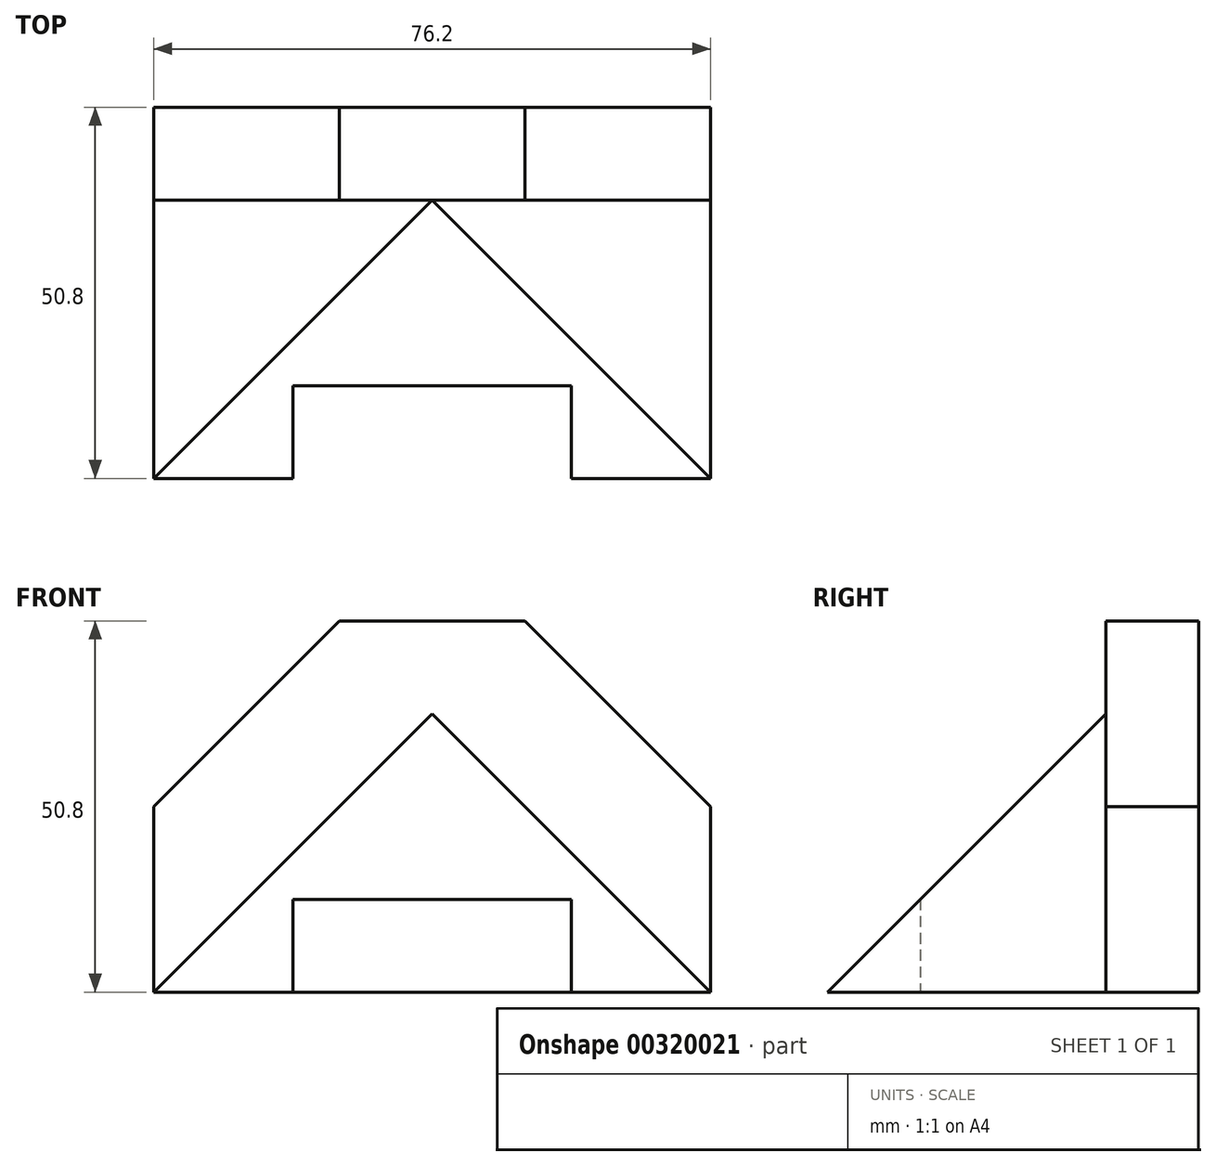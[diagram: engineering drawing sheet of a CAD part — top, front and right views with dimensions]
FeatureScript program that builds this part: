
annotation { "Feature Type Name" : "Feature", "Feature Type Description" : "" }
export const myFeature = defineFeature(function(context is Context, id is Id, definition is map)
    precondition{}
    {
        {
            var Q0;
            Q0=qCreatedBy(makeId("Front.planeOp"),FACE);
            var sketch = newSketch(context, id + "F0", { "sketchPlane" : qUnion([Q0])});
            skLineSegment(sketch, "E0", {"start": v(0, 0) * mm, "end": v(0, 25.4) * mm});
            skLineSegment(sketch, "E1", {"start": v(0, 25.4) * mm, "end": v(25.4, 50.8) * mm});
            skLineSegment(sketch, "E2", {"start": v(25.4, 50.8) * mm, "end": v(50.8, 50.8) * mm});
            skLineSegment(sketch, "E3", {"start": v(50.8, 50.8) * mm, "end": v(76.2, 25.4) * mm});
            skLineSegment(sketch, "E4", {"start": v(76.2, 25.4) * mm, "end": v(76.2, 0) * mm});
            skLineSegment(sketch, "E5", {"start": v(76.2, 0) * mm, "end": v(0, 0) * mm});
            skSolve(sketch);
        }
        {
            var Q0;
            Q0 = qSketchRegion(id + "F0", true);
            extrude(context, id + "F1", {"entities" : qUnion([Q0]), "depth" : 12.7 * mm});
        }
        {
            var Q0;
            Q0=makeQuery(id+"F1.opExtrude","CAP_FACE",FACE,{"disambiguationData":[OSD([sQuery(id+"F0.wireOp",EDGE,"E0"),sQuery(id+"F0.wireOp",EDGE,"E1"),sQuery(id+"F0.wireOp",EDGE,"E2"),sQuery(id+"F0.wireOp",EDGE,"E3"),sQuery(id+"F0.wireOp",EDGE,"E4"),sQuery(id+"F0.wireOp",EDGE,"E5")])],"isStart":false});
            var sketch = newSketch(context, id + "F2", { "sketchPlane" : qUnion([Q0])});
            skLineSegment(sketch, "E6", {"start": v(0, 0) * mm, "end": v(76.2, 0) * mm});
            skLineSegment(sketch, "E7", {"start": v(76.2, 0) * mm, "end": v(38.1, 38.1) * mm});
            skLineSegment(sketch, "E8", {"start": v(38.1, 38.1) * mm, "end": v(0, 0) * mm});
            skSolve(sketch);
        }
        {
            var Q0;
            Q0 = qSketchRegion(id + "F2", true);
            extrude(context, id + "F3", {"entities" : qUnion([Q0]), "operationType" : NewBodyOperationType.ADD, "depth" : 38.1 * mm});
        }
        {
            var Q0;
            Q0=makeQuery(id+"F1.opExtrude","SWEPT_FACE",FACE,{"disambiguationData":[OSD([sQuery(id+"F0.wireOp",EDGE,"E4")])]});
            var sketch = newSketch(context, id + "F4", { "sketchPlane" : qUnion([Q0])});
            skLineSegment(sketch, "E9", {"start": v(-50.8, 0) * mm, "end": v(-12.7, 38.1) * mm});
            skLineSegment(sketch, "E10", {"start": v(-12.7, 38.1) * mm, "end": v(-50.8, 38.1) * mm});
            skLineSegment(sketch, "E11", {"start": v(-50.8, 38.1) * mm, "end": v(-50.8, 0) * mm});
            skSolve(sketch);
        }
        {
            var Q0;
            Q0 = qSketchRegion(id + "F4", true);
            extrude(context, id + "F5", {"entities" : qUnion([Q0]), "operationType" : NewBodyOperationType.REMOVE, "endBound" : BoundingType.THROUGH_ALL, "oppositeDirection" : true, "depth" : 25.4 * mm});
        }
        {
            var Q0;
            Q0=makeQuery(id+"F3.boolean.opBoolean","MERGE",FACE,{"derivedFrom":[makeQuery(id+"F1.opExtrude","SWEPT_FACE",FACE,{"disambiguationData":[OSD([sQuery(id+"F0.wireOp",EDGE,"E5")])]}),makeQuery(id+"F3.opExtrude","SWEPT_FACE",FACE,{"disambiguationData":[OSD([sQuery(id+"F2.wireOp",EDGE,"E6")])]})]});
            var sketch = newSketch(context, id + "F6", { "sketchPlane" : qUnion([Q0])});
            skLineSegment(sketch, "E12", {"start": v(19.05, 50.8) * mm, "end": v(19.05, 38.1) * mm});
            skLineSegment(sketch, "E13", {"start": v(19.05, 38.1) * mm, "end": v(57.15, 38.1) * mm});
            skLineSegment(sketch, "E14", {"start": v(57.15, 38.1) * mm, "end": v(57.15, 50.8) * mm});
            skSolve(sketch);
        }
        {
            var Q0;
            Q0 = qSketchRegion(id + "F6", true);
            var Q1;
            {var subQ0=sQuery(id+"F6.wireOp",EDGE,"E12");Q1=makeQuery(id+"F6.imprint","IMPRINT",FACE,{"disambiguationData":[TD([[makeQuery(id+"F6.imprint","IMPRINT",EDGE,{"derivedFrom":subQ0}),1.0]])]});}
            extrude(context, id + "F7", {"entities" : qUnion([Q0, Q1]), "operationType" : NewBodyOperationType.REMOVE, "endBound" : BoundingType.THROUGH_ALL, "oppositeDirection" : true, "depth" : 25.4 * mm});
        }
    });
